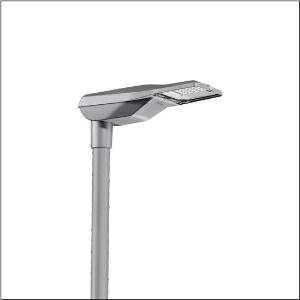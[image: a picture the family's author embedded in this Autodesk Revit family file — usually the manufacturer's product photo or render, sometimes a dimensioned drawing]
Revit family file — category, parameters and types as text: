
# Revit family: streetlight_sl_21_iq_micro___st0_8a_5xe1c61d08cb_7ac8
name_source: partatom
category: Lighting Fixtures
units: mm (PartAtom-declared; Revit-internal decimal feet)

## family parameters
Cut with Voids When Loaded = No
Host = Face
Light Source = No
Part Type = Normal
Room Calculation Point = No
Round Connector Dimension = Use Diameter
Shared = No

## types (1)
- --- (1 x LED, 2570 lm, 19.4 W, 2700K)
    Apparent Load = 19 VA
    CIE Flux Codes = 38 75 97 100 100
    Color Rendering = 70
    Color Temperature = 2700K
    Default Elevation = 1800 mm
    Description = Streetlight SL 21 iQ micro, mast luminaire, primary light control with lens, of PMMA, primary optical cover: cover, of toughened safety glass, transparent, light distribution: ST0.8a, light emission: direct distribution, primary light characteristic: asymmetric, installation type: post-top, side-entry, LED, High Power LED, rated luminous flux: 2.570lm, luminous efficacy: 133lm/W, light colour: 727, colour temperature: 2700K, control: Auto-Match, Temp-Guard, Lumen-Switch, Night-Set, Smart-Wire, Light-Fading, Desk-Remote (wireless, voltage-free reading and setting of iQ features in the workshop via application-optimized NFC function/RFID function), optimised constant luminous flux control (CLO 2.0), presetting dimming linear, mains connection: 220..240V, AC, 50/60Hz, start of lifetime: 19W, end of service life: 20W, reduction: 10W, luminaire housing, of diecast aluminium, powder-coated, Siteco® metallic grey (DB 702S), corrosivity category C5 mid according to DIN EN ISO 12944, please order mast flange separately, inclination adjustable: 0°, 5°, 10°, 15°, sealing non-destructively replaceable, multi-level sealing system, length: 528mm, width: 235mm, height: 110mm, mast flange for spigot size: 42mm (side-entry): 5XC10008XM4, 60/48mm (side-entry/post-top): 5XC10108XM2, 76/60mm (side-entry/post-top): 5XC10108XM1, protection rating (complete): IP66, insulation class (complete): insulation class II (safety insulation), certification: CE, ENEC, ENEC+, VDE, impact resistance: IK09, permissible operating ambient temperature for outdoor applications: -40..+50°C, standard-compliant lighting for roads and squares, packaging unit: 1 piece

Light Distribution: ST0.8a
    Height = 110 mm
    Lamp = 1 x LED
    Lamp Light Flux = 2570 lm
    Lamp Power = 19.4 W
    Lamp count = 1
    Length = 528 mm
    Luminous efficacy = 132 lm/W
    Manufacturer = Siteco
    ModVariant = No
    Model = 5XE1C61D08CB
    Number of Poles = 1
    OnlyDefault = Yes
    Power Factor = 1
    Product Name = Streetlight SL 21 iQ micro | ST0.8a
    Product group = mast luminaire | pylon top
    ProductGroupID = 6100
    Protection Class = Protection class II
    Protection Degree = IP 66
    RLX_Detail_Level = 1
    RLX_Emergency_Light_Flux = 0 lm
    RLX_Emergency_Type = 0
    RLX_Emergency_Type_DB = No
    RlxData = <blob elided: 98709 chars, md5=ed292d1c>
    Socket = socket
    Standby Power = 0 W
    System Light Flux = 2570 lm
    System Power = 19 W
    Type Comments = factory setting: luminous flux: 100 % | dim-lin: 254 | 387 mA
    Type Image = l_1006881.jpg
    URL = http://relux.com
    VarID = @adj_087689
    Voltage = 0 V
    Weight = 0.00 kg
    Width = 235 mm

## geometry (parser evidence)
native form markers: Blend x4, Sweep x11
no freeform markers — native parametric forms only
